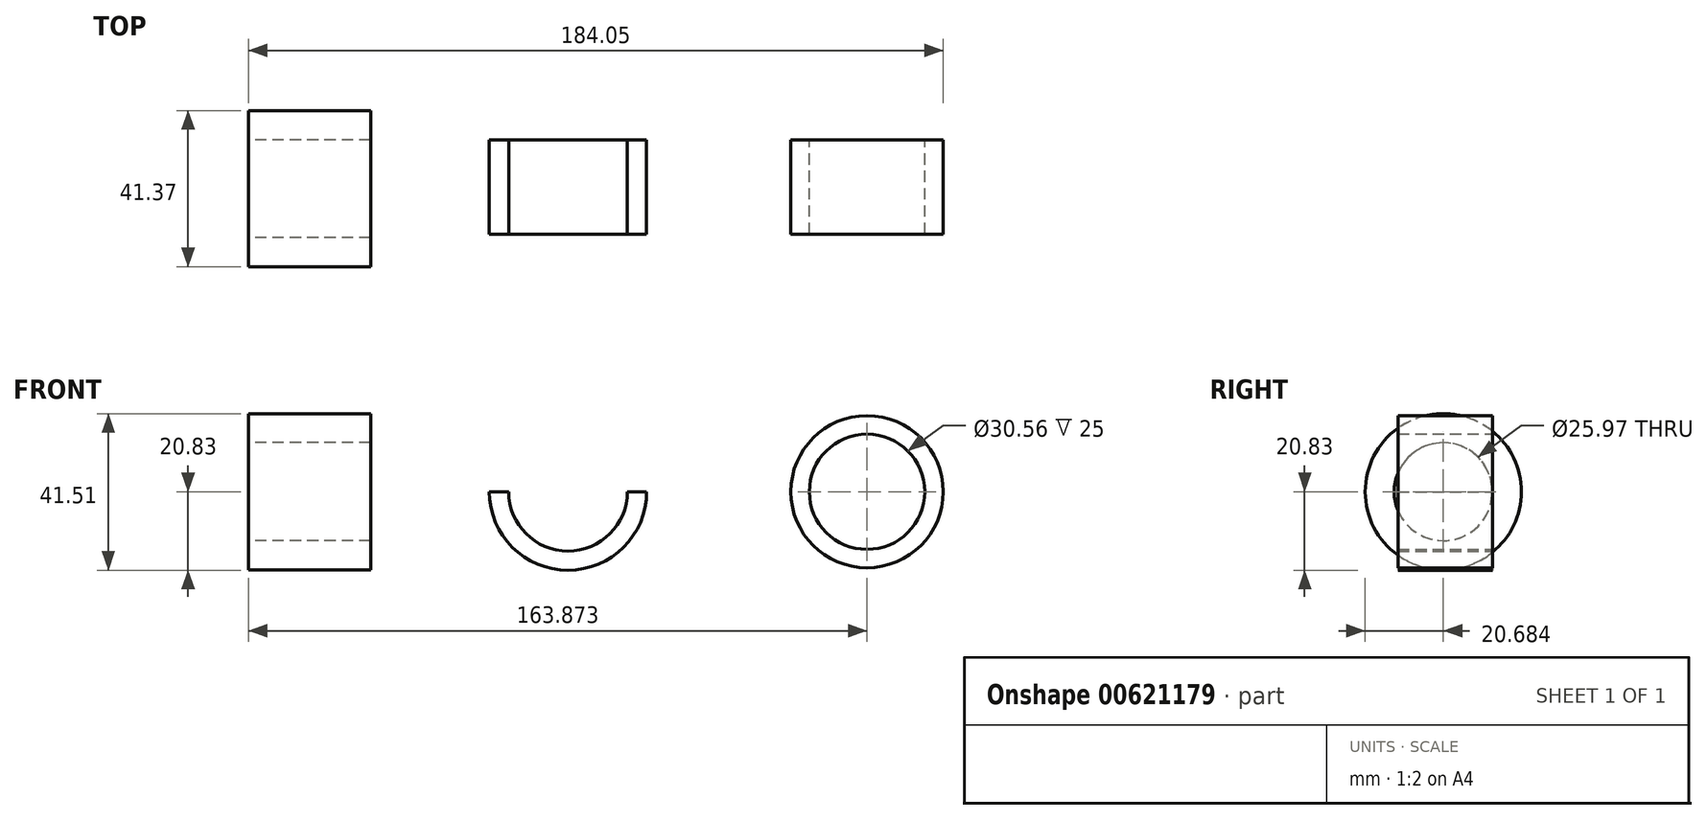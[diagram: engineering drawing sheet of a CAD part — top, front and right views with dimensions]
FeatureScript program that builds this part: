
annotation { "Feature Type Name" : "Feature", "Feature Type Description" : "" }
export const myFeature = defineFeature(function(context is Context, id is Id, definition is map)
    precondition{}
    {
        {
            var Q0;
            Q0=qCreatedBy(makeId("Top.planeOp"),FACE);
            var sketch = newSketch(context, id + "F0", { "sketchPlane" : qUnion([Q0])});
            skLineSegment(sketch, "E0", {"start": v(-51.17, 0) * mm, "end": v(-18.82, 0) * mm});
            skLineSegment(sketch, "E1", {"start": v(-18.82, 0) * mm, "end": v(-18.82, 7.7) * mm});
            skLineSegment(sketch, "E2", {"start": v(-18.82, 7.7) * mm, "end": v(-51.17, 7.7) * mm});
            skLineSegment(sketch, "E3", {"start": v(-51.17, 7.7) * mm, "end": v(-51.17, -12.99) * mm});
            skLineSegment(sketch, "E4", {"start": v(-51.17, -12.99) * mm, "end": v(-18.25, -12.99) * mm});
            skSolve(sketch);
        }
        {
            var Q0;
            Q0 = qSketchRegion(id + "F0", true);
            var Q1;
            Q1=sQuery(id+"F0.wireOp",EDGE,"E4");
            revolve(context, id + "F1", {"entities" : qUnion([Q0]), "axis" : qUnion([Q1]), "revolveType" : RevolveType.FULL});
        }
        {
            var Q0;
            Q0=qCreatedBy(makeId("Front.planeOp"),FACE);
            var sketch = newSketch(context, id + "F2", { "sketchPlane" : qUnion([Q0])});
            skArc(sketch, "E5", {"start": v(54.31, 0) * mm, "mid": v(33.49, -20.83) * mm, "end": v(12.66, 0) * mm});
            skArc(sketch, "E6", {"start": v(49.2, 0) * mm, "mid": v(33.49, -15.72) * mm, "end": v(17.76, 0) * mm});
            skLineSegment(sketch, "E7", {"start": v(12.66, 0) * mm, "end": v(17.76, 0) * mm});
            skLineSegment(sketch, "E8", {"start": v(49.2, 0) * mm, "end": v(54.31, 0) * mm});
            skSolve(sketch);
        }
        {
            var Q0;
            Q0 = qSketchRegion(id + "F2", true);
            extrude(context, id + "F3", {"entities" : qUnion([Q0]), "depth" : 25 * mm, "offsetDistance" : 25 * mm});
        }
        {
            var Q0;
            Q0=qCreatedBy(makeId("Front.planeOp"),FACE);
            var sketch = newSketch(context, id + "F4", { "sketchPlane" : qUnion([Q0])});
            skCircle(sketch, "E9", {"center": v(112.7, 0) * mm, "radius": 20.17 * mm});
            skCircle(sketch, "E10", {"center": v(112.7, 0) * mm, "radius": 15.28 * mm});
            skSolve(sketch);
        }
        {
            var Q0;
            Q0 = qSketchRegion(id + "F4", true);
            extrude(context, id + "F5", {"entities" : qUnion([Q0]), "depth" : 25 * mm, "offsetDistance" : 25 * mm});
        }
    });
